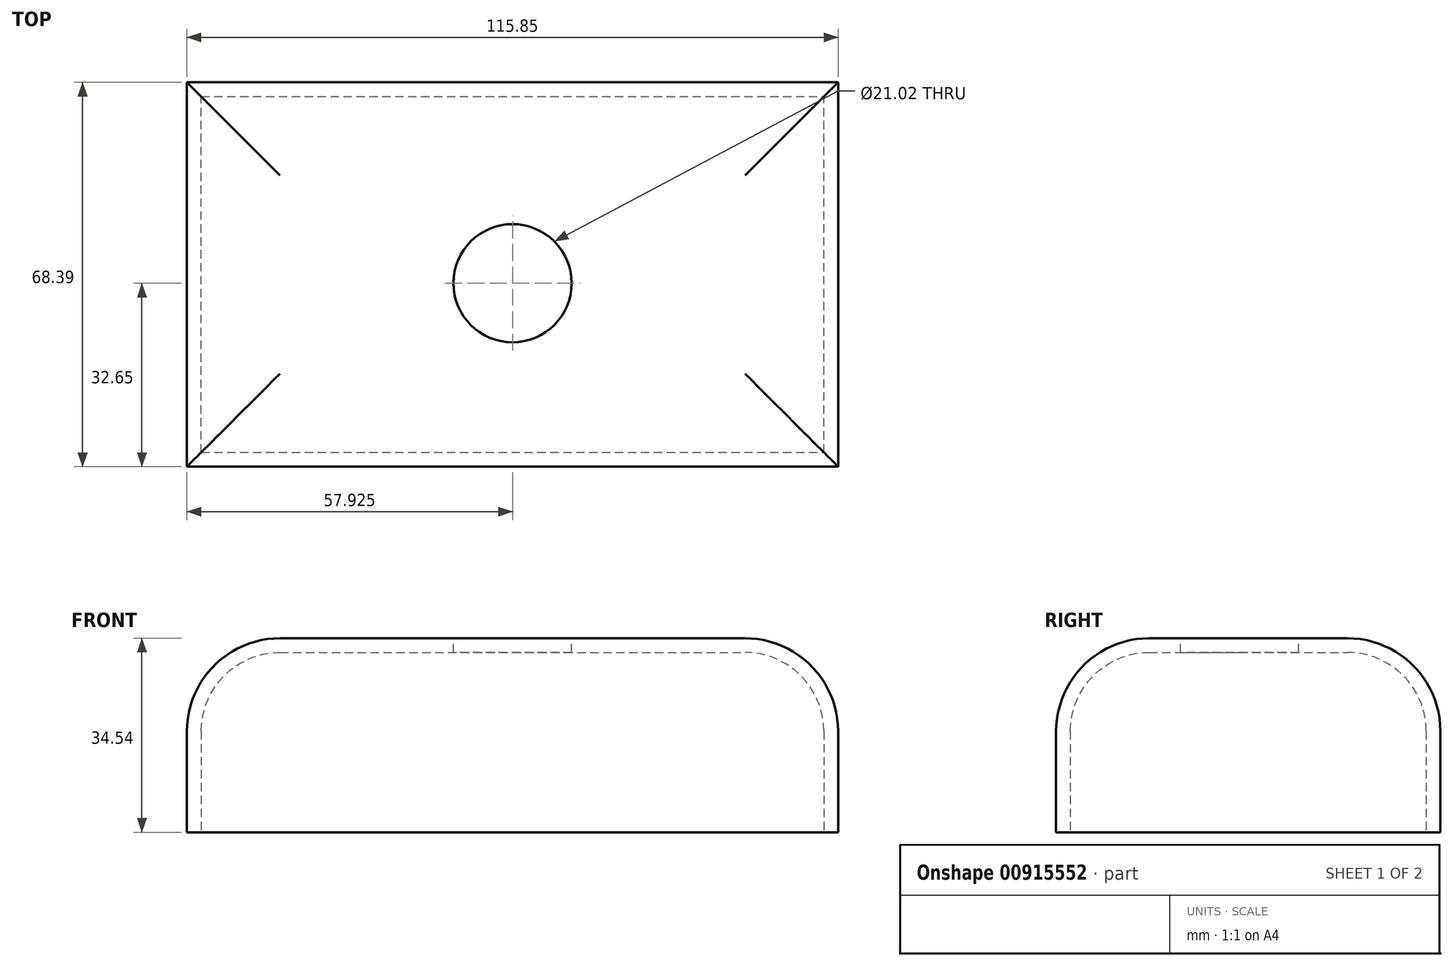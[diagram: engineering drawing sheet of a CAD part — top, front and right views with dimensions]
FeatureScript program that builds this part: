
annotation { "Feature Type Name" : "Feature", "Feature Type Description" : "" }
export const myFeature = defineFeature(function(context is Context, id is Id, definition is map)
    precondition{}
    {
        {
            var Q0;
            Q0=qCreatedBy(makeId("Top.planeOp"),FACE);
            var sketch = newSketch(context, id + "F0", { "sketchPlane" : qUnion([Q0])});
            skLineSegment(sketch, "E0.bottom", {"start": v(0, 0) * mm, "end": v(115.85, 0) * mm});
            skLineSegment(sketch, "E0.top", {"start": v(0, 68.4) * mm, "end": v(115.85, 68.4) * mm});
            skLineSegment(sketch, "E0.left", {"start": v(0, 0) * mm, "end": v(0, 68.4) * mm});
            skLineSegment(sketch, "E0.right", {"start": v(115.85, 0) * mm, "end": v(115.85, 68.4) * mm});
            skSolve(sketch);
        }
        {
            var Q0;
            Q0=makeQuery(id+"F0.imprint","IMPRINT",FACE,{"disambiguationData":[TD([[makeQuery(id+"F0.imprint","IMPRINT",EDGE,{"derivedFrom":sQuery(id+"F0.wireOp",EDGE,"E0.bottom")}),1.0]])]});
            extrude(context, id + "F1", {"entities" : qUnion([Q0]), "depth" : 34.54 * mm, "offsetDistance" : 25.4 * mm});
        }
        {
            var Q0;
            Q0=makeQuery(id+"F1.opExtrude","CAP_FACE",FACE,{"disambiguationData":[OSD([sQuery(id+"F0.wireOp",EDGE,"E0.bottom"),sQuery(id+"F0.wireOp",EDGE,"E0.top"),sQuery(id+"F0.wireOp",EDGE,"E0.left"),sQuery(id+"F0.wireOp",EDGE,"E0.right")])],"isStart":false});
            fillet(context, id + "F2", {"entities" : qUnion([Q0]), "radius" : 16.56 * mm, "tangentPropagation" : true, "allowEdgeOverflow" : false});
        }
        {
            var Q0;
            Q0=makeQuery(id+"F1.opExtrude","CAP_FACE",FACE,{"disambiguationData":[OSD([sQuery(id+"F0.wireOp",EDGE,"E0.bottom"),sQuery(id+"F0.wireOp",EDGE,"E0.top"),sQuery(id+"F0.wireOp",EDGE,"E0.left"),sQuery(id+"F0.wireOp",EDGE,"E0.right")])],"isStart":true});
            shell(context, id + "F3", {"entities" : qUnion([Q0]), "thickness" : 2.54 * mm});
        }
        {
            var Q0;
            Q0=makeQuery(id+"F1.opExtrude","CAP_FACE",FACE,{"disambiguationData":[OSD([sQuery(id+"F0.wireOp",EDGE,"E0.bottom"),sQuery(id+"F0.wireOp",EDGE,"E0.top"),sQuery(id+"F0.wireOp",EDGE,"E0.left"),sQuery(id+"F0.wireOp",EDGE,"E0.right")])],"isStart":false});
            var sketch = newSketch(context, id + "F4", { "sketchPlane" : qUnion([Q0])});
            skCircle(sketch, "E1", {"center": v(57.93, 32.65) * mm, "radius": 10.51 * mm});
            skPoint(sketch, "E1.centerSnap0", {"position": v(57.93, 16.56) * mm});
            skSolve(sketch);
        }
        {
            var Q0;
            Q0=makeQuery(id+"F4.imprint","IMPRINT",FACE,{"disambiguationData":[TD([[makeQuery(id+"F4.imprint","IMPRINT",EDGE,{"derivedFrom":sQuery(id+"F4.wireOp",EDGE,"E1")}),1.0]])]});
            extrude(context, id + "F5", {"entities" : qUnion([Q0]), "operationType" : NewBodyOperationType.REMOVE, "oppositeDirection" : true, "depth" : 25.4 * mm, "offsetDistance" : 25.4 * mm});
        }
    });
